MODEL slx_82d3541175fb
CONFIG AbsTol = auto
CONFIG EnableMultiTasking = off
CONFIG FixedStep = auto
CONFIG MaxStep = auto
CONFIG MinStep = auto
CONFIG RelTol = 1e-3
CONFIG SampleTimeConstraint = Unconstrained
CONFIG SolverName = VariableStepAuto
CONFIG StartTime = 0.0
CONFIG StopTime = 7
BLOCK [Reference] AC Voltage Source3  REF=spsACVoltageSourceLib/AC Voltage Source
  Commented = on
  LibrarySourceBlock = sps_lib/Sources/AC Voltage Source
  NameLocation = left
  SourceBlock = spsACVoltageSourceLib/AC Voltage Source
  SourceType = AC Voltage Source
BLOCK [BusSelector] Bus Selector1
  OutputSignals = Electrical torque Te (n m),Speed wm (rad/s)
BLOCK [Constant] CCW Direction
  Value = 0
BLOCK [Constant] CW Direction
BLOCK [Constant] Constant2
  Value = 0.6
BLOCK [Reference] Current Measurement  REF=spsCurrentMeasurementLib/Current Measurement
  LibrarySourceBlock = sps_lib/Sensors and Measurements/Current Measurement
  SourceBlock = spsCurrentMeasurementLib/Current Measurement
  SourceType = Current Measurement
  UserDataPersistent = on
BLOCK [Reference] Current Measurement1  REF=spsCurrentMeasurementLib/Current Measurement
  Commented = on
  LibrarySourceBlock = sps_lib/Sensors and Measurements/Current Measurement
  SourceBlock = spsCurrentMeasurementLib/Current Measurement
  SourceType = Current Measurement
  UserDataPersistent = on
BLOCK [Reference] Current Measurement2  REF=spsCurrentMeasurementLib/Current Measurement
  LibrarySourceBlock = sps_lib/Sensors and Measurements/Current Measurement
  SourceBlock = spsCurrentMeasurementLib/Current Measurement
  SourceType = Current Measurement
  UserDataPersistent = on
BLOCK [Reference] DC Machine1  REF=spsDCMachineLib/DC Machine
  LibrarySourceBlock = sps_lib/Electrical Machines/DC Machine
  SourceBlock = spsDCMachineLib/DC Machine
  SourceType = DC machine
BLOCK [Reference] DC Voltage Source  REF=spsDCVoltageSourceLib/DC Voltage Source
  LibrarySourceBlock = sps_lib/Sources/DC Voltage Source
  NameLocation = right
  SourceBlock = spsDCVoltageSourceLib/DC Voltage Source
  SourceType = DC Voltage Source
BLOCK [Reference] DC Voltage Source1  REF=spsDCVoltageSourceLib/DC Voltage Source
  LibrarySourceBlock = sps_lib/Sources/DC Voltage Source
  SourceBlock = spsDCVoltageSourceLib/DC Voltage Source
  SourceType = DC Voltage Source
BLOCK [Reference] Diode1  REF=spsDiodeLib/Diode
  LibrarySourceBlock = sps_lib/Power Electronics/Diode
  NameLocation = right
  SourceBlock = spsDiodeLib/Diode
  SourceType = Diode
BLOCK [Reference] Diode2  REF=spsDiodeLib/Diode
  LibrarySourceBlock = sps_lib/Power Electronics/Diode
  NameLocation = right
  SourceBlock = spsDiodeLib/Diode
  SourceType = Diode
BLOCK [Reference] Diode3  REF=spsDiodeLib/Diode
  LibrarySourceBlock = sps_lib/Power Electronics/Diode
  NameLocation = right
  SourceBlock = spsDiodeLib/Diode
  SourceType = Diode
BLOCK [Reference] Diode4  REF=spsDiodeLib/Diode
  LibrarySourceBlock = sps_lib/Power Electronics/Diode
  NameLocation = right
  SourceBlock = spsDiodeLib/Diode
  SourceType = Diode
BLOCK [Reference] Diode5  REF=spsDiodeLib/Diode
  Commented = on
  LibrarySourceBlock = sps_lib/Power Electronics/Diode
  NameLocation = right
  SourceBlock = spsDiodeLib/Diode
  SourceType = Diode
BLOCK [Reference] Diode6  REF=spsDiodeLib/Diode
  Commented = on
  LibrarySourceBlock = sps_lib/Power Electronics/Diode
  NameLocation = right
  SourceBlock = spsDiodeLib/Diode
  SourceType = Diode
BLOCK [Reference] Diode7  REF=spsDiodeLib/Diode
  Commented = on
  LibrarySourceBlock = sps_lib/Power Electronics/Diode
  NameLocation = right
  SourceBlock = spsDiodeLib/Diode
  SourceType = Diode
BLOCK [Reference] Diode8  REF=spsDiodeLib/Diode
  Commented = on
  LibrarySourceBlock = sps_lib/Power Electronics/Diode
  NameLocation = right
  SourceBlock = spsDiodeLib/Diode
  SourceType = Diode
BLOCK [Reference] Ground  REF=spsGroundLib/Ground
  LibrarySourceBlock = sps_lib/Utilities/Ground
  NameLocation = right
  SourceBlock = spsGroundLib/Ground
  SourceType = Ground
BLOCK [ManualSwitch] Manual Switch
BLOCK [ManualSwitch] Manual Switch1
  CurrentSetting = 0
BLOCK [Reference] Mosfet1  REF=spsMosfetLib/Mosfet
  LibrarySourceBlock = sps_lib/Power Electronics/Mosfet
  NameLocation = left
  SourceBlock = spsMosfetLib/Mosfet
  SourceType = Mosfet
BLOCK [Reference] Mosfet2  REF=spsMosfetLib/Mosfet
  LibrarySourceBlock = sps_lib/Power Electronics/Mosfet
  NameLocation = left
  SourceBlock = spsMosfetLib/Mosfet
  SourceType = Mosfet
BLOCK [Reference] Mosfet3  REF=spsMosfetLib/Mosfet
  LibrarySourceBlock = sps_lib/Power Electronics/Mosfet
  NameLocation = left
  SourceBlock = spsMosfetLib/Mosfet
  SourceType = Mosfet
BLOCK [Reference] Mosfet4  REF=spsMosfetLib/Mosfet
  LibrarySourceBlock = sps_lib/Power Electronics/Mosfet
  NameLocation = left
  SourceBlock = spsMosfetLib/Mosfet
  SourceType = Mosfet
BLOCK [Logic] NOT
  AllPortsSameDT = off
  IconShape = distinctive
  Operator = NOT
  OutDataTypeStr = boolean
BLOCK [Reference] PWM Generator  REF=eePwmGenerator/PWM Generator
  LibrarySourceBlock = ee_sl_lib/Pulse Width
Modulation/PWM Generator
  SourceBlock = eePwmGenerator/PWM Generator
  SourceType = PWM Generator
BLOCK [Product] Product
BLOCK [Product] Product1
BLOCK [Reference] Ramp  REF=simulink/Sources/Ramp
  NameLocation = left
  SourceBlock = simulink/Sources/Ramp
  SourceType = Ramp
BLOCK [Reference] Ramp1  REF=simulink/Sources/Ramp
  SourceBlock = simulink/Sources/Ramp
  SourceType = Ramp
BLOCK [Saturate] Saturation
  LowerLimit = 0
  NameLocation = left
  UpperLimit = 10
BLOCK [Saturate] Saturation1
  LowerLimit = 0
  UpperLimit = 0.8
BLOCK [Scope] Scope
  ActiveDisplayYMaximum = 127.17519359460283
  ActiveDisplayYMinimum = -14.130577066066978
  DataLoggingVariableName = ScopeData2
  Floating = off
  GraphicalSettings = {"AxesScalingProperties":{"AlignXAxis":"Center","AlignYAxis":"Center","AutoScaleXAxisLimits":false,"AxesScaling":"Manual","AxesScalingNumUpdates":10,"ExpandOnly":true,"ScaleAxesLimitsAtStop":false,"XAxisDataRange":100,"YAxisDataRange":80},"DisplayProperties":{"ColorOrder":["auto","auto","auto","auto","auto","auto","auto","auto","auto","auto","auto","auto","auto","auto","auto","auto","auto","auto",...<+2178ch>
  MultipleDisplayCache = [{"MaxYLimMag":127.17519359460283,"MaxYLimReal":127.17519359460283,"MinYLimMag":0,"MinYLimReal":-14.130577066066978,"PlotAsMagnitudePhase":false,"ShowGrid":true,"ShowLegend":true,"Title":"%<SignalLabel>","YLabel":""}]
  NameLocation = left
  NumInputPorts = 1
  ScopeFrameLocation = window
  ShowLegend = on
  WasSavedAsWebScope = on
  WindowPosition = [1.000000,41.000000,1920.000000,1017.000000,]
BLOCK [Scope] Scope1
  ActiveDisplayYMaximum = 205.7174886404658
  ActiveDisplayYMinimum = 197.20667546347846
  Floating = off
  GraphicalSettings = {"AxesScalingProperties":{"AlignXAxis":"Center","AlignYAxis":"Center","AutoScaleXAxisLimits":false,"AxesScaling":"Manual","AxesScalingNumUpdates":10,"ExpandOnly":true,"ScaleAxesLimitsAtStop":false,"XAxisDataRange":100,"YAxisDataRange":80},"DisplayProperties":{"ColorOrder":["auto","auto","auto","auto","auto","auto","auto","auto","auto","auto","auto","auto","auto","auto","auto","auto","auto","auto",...<+2026ch>
  MultipleDisplayCache = [{"MaxYLimMag":229.0419020090381,"MaxYLimReal":205.7174886404658,"MinYLimMag":0,"MinYLimReal":197.20667546347846,"PlotAsMagnitudePhase":false,"ShowGrid":true,"ShowLegend":false,"Title":"%<SignalLabel>","YLabel":""}]
  NumInputPorts = 1
  ScopeFrameLocation = window
  WasSavedAsWebScope = on
  WindowPosition = [0.000000,32.000000,1536.000000,801.000000,]
BLOCK [Scope] Scope12
  ActiveDisplayYMaximum = 9.5444979024542747
  ActiveDisplayYMinimum = -4.3267096598487811
  DataLoggingVariableName = ScopeData11
  Floating = off
  GraphicalSettings = {"Style":{"BackgroundColor":[0.12941176470588237,0.12941176470588237,0.12941176470588237],"AxesColor":[0.07058823529411765,0.07058823529411765,0.07058823529411765],"LabelsColor":[0.8509803921568627,0.8509803921568627,0.8509803921568627],"PreserveColors":false,"Visible":[true],"LineStyle":["-"],"LineWidth":[1.5],"BarWidth":[0.9],"LineColor":["auto"],"LineFaceAlpha":[1],"LineEdgeAlpha":[1],"Marker":...<+2017ch>
  MultipleDisplayCache = [{"MaxYLimMag":127.0240272759662,"MaxYLimReal":9.5444979024542747,"MinYLimMag":0,"MinYLimReal":-4.3267096598487811,"PlotAsMagnitudePhase":false,"ShowGrid":true,"ShowLegend":false,"Title":"%<SignalLabel>","YLabel":""}]
  NameLocation = right
  NumInputPorts = 1
  ScopeFrameLocation = window
  WasSavedAsWebScope = on
  WindowPosition = [0.000000,32.000000,1536.000000,801.000000,]
BLOCK [Scope] Scope2
  ActiveDisplayYMaximum = 25.20951403026401
  ActiveDisplayYMinimum = -226.88562627237616
  DataLoggingVariableName = ScopeData3
  Floating = off
  GraphicalSettings = {"Style":{"BackgroundColor":[0.12941176470588237,0.12941176470588237,0.12941176470588237],"AxesColor":[0.07058823529411765,0.07058823529411765,0.07058823529411765],"LabelsColor":[0.8509803921568627,0.8509803921568627,0.8509803921568627],"PreserveColors":false,"Visible":[true,true],"LineStyle":["-","-"],"LineWidth":[1.5,1.5],"BarWidth":[0.9,0.9],"LineColor":["auto","auto"],"LineFaceAlpha":[1,1],"Li...<+2069ch>
  MultipleDisplayCache = [{"MaxYLimMag":226.88562627237616,"MaxYLimReal":25.20951403026401,"MinYLimMag":0,"MinYLimReal":-226.88562627237616,"PlotAsMagnitudePhase":false,"ShowGrid":true,"ShowLegend":false,"Title":"%<SignalLabel>","YLabel":""}]
  NameLocation = right
  NumInputPorts = 1
  ScopeFrameLocation = window
  WasSavedAsWebScope = on
  WindowPosition = [488.000000,222.000000,560.000000,420.000000,]
BLOCK [Scope] Scope3
  ActiveDisplayYMaximum = 0.45210221887226021
  ActiveDisplayYMinimum = -4.2782265526615753
  DataLoggingVariableName = ScopeData4
  Floating = off
  GraphicalSettings = {"Style":{"BackgroundColor":[0.12941176470588237,0.12941176470588237,0.12941176470588237],"AxesColor":[0.07058823529411765,0.07058823529411765,0.07058823529411765],"LabelsColor":[0.8509803921568627,0.8509803921568627,0.8509803921568627],"PreserveColors":false,"Visible":[true,false,true,true,true,true,true],"LineStyle":["-","-","-","-","-","-","-"],"LineWidth":[1.5,1.5,1.5,1.5,1.5,1.5,1.5],"BarWidt...<+2576ch>
  MultipleDisplayCache = [{"MaxYLimMag":4.2572958943804515,"MaxYLimReal":0.45210221887226021,"MinYLimMag":0,"MinYLimReal":-4.2782265526615753,"PlotAsMagnitudePhase":false,"ShowGrid":true,"ShowLegend":true,"Title":"%<SignalLabel>","YLabel":""}]
  NameLocation = left
  NumInputPorts = 1
  ScopeFrameLocation = window
  ShowLegend = on
  WasSavedAsWebScope = on
  WindowPosition = [680.000000,330.000000,560.000000,420.000000,]
BLOCK [Scope] Scope4
  ActiveDisplayYMaximum = 190.37679133211168
  ActiveDisplayYMinimum = -17.897638486431848
  DataLoggingVariableName = ScopeData1
  Floating = off
  GraphicalSettings = {"AxesScalingProperties":{"AlignXAxis":"Center","AlignYAxis":"Center","AutoScaleXAxisLimits":false,"AxesScaling":"Manual","AxesScalingNumUpdates":10,"ExpandOnly":true,"ScaleAxesLimitsAtStop":false,"XAxisDataRange":100,"YAxisDataRange":80},"DisplayProperties":{"ColorOrder":["auto","auto","auto","auto","auto","auto","auto","auto","auto","auto","auto","auto","auto","auto","auto","auto","auto","auto",...<+2048ch>
  MultipleDisplayCache = [{"MaxYLimMag":239.23513324584667,"MaxYLimReal":190.37679133211168,"MinYLimMag":0,"MinYLimReal":-17.897638486431848,"PlotAsMagnitudePhase":false,"ShowGrid":true,"ShowLegend":false,"Title":"%<SignalLabel>","YLabel":""}]
  NumInputPorts = 1
  ScopeFrameLocation = window
  WasSavedAsWebScope = on
  WindowPosition = [1.000000,41.000000,1920.000000,1017.000000,]
BLOCK [Scope] Scope5
  ActiveDisplayYMaximum = 7.0075960496809362
  ActiveDisplayYMinimum = -1.20703950016334
  DataLoggingVariableName = ScopeData6
  Floating = off
  GraphicalSettings = {"Style":{"BackgroundColor":[0.12941176470588237,0.12941176470588237,0.12941176470588237],"AxesColor":[0.07058823529411765,0.07058823529411765,0.07058823529411765],"LabelsColor":[0.8509803921568627,0.8509803921568627,0.8509803921568627],"PreserveColors":false,"Visible":[true,true],"LineStyle":["-","-"],"LineWidth":[1.5,1.5],"BarWidth":[0.9,0.9],"LineColor":["auto","auto"],"LineFaceAlpha":[1,1],"Li...<+2168ch>
  MultipleDisplayCache = [{"MaxYLimMag":126.86904472662312,"MaxYLimReal":7.0075960496809362,"MinYLimMag":0,"MinYLimReal":-1.20703950016334,"PlotAsMagnitudePhase":false,"ShowGrid":true,"ShowLegend":false,"Title":"%<SignalLabel>","YLabel":""}]
  NameLocation = left
  NumInputPorts = 1
  ScopeFrameLocation = window
  WasSavedAsWebScope = on
  WindowPosition = [0.000000,32.000000,1536.000000,801.000000,]
BLOCK [Scope] Scope6
  ActiveDisplayYMaximum = 74.662265345837412
  ActiveDisplayYMinimum = -7.1846961495374888
  DataLoggingVariableName = ScopeData5
  Floating = off
  GraphicalSettings = {"Style":{"BackgroundColor":[0.12941176470588237,0.12941176470588237,0.12941176470588237],"AxesColor":[0.07058823529411765,0.07058823529411765,0.07058823529411765],"LabelsColor":[0.8509803921568627,0.8509803921568627,0.8509803921568627],"PreserveColors":false,"Visible":[true],"LineStyle":["-"],"LineWidth":[1.5],"BarWidth":[0.9],"LineColor":["auto"],"LineFaceAlpha":[1],"LineEdgeAlpha":[1],"Marker":...<+2015ch>
  MultipleDisplayCache = [{"MaxYLimMag":74.662265345837412,"MaxYLimReal":74.662265345837412,"MinYLimMag":0,"MinYLimReal":-7.1846961495374888,"PlotAsMagnitudePhase":false,"ShowGrid":true,"ShowLegend":false,"Title":"%<SignalLabel>","YLabel":""}]
  NumInputPorts = 1
  ScopeFrameLocation = window
  WasSavedAsWebScope = on
  WindowPosition = [1.000000,41.000000,1920.000000,1017.000000,]
BLOCK [Scope] Scope7
  ActiveDisplayYMaximum = 546.71556577016588
  ActiveDisplayYMinimum = -568.37134406736811
  Commented = on
  DataLoggingVariableName = ScopeData7
  Floating = off
  GraphicalSettings = {"AxesScalingProperties":{"AlignXAxis":"Center","AlignYAxis":"Center","AutoScaleXAxisLimits":false,"AxesScaling":"Manual","AxesScalingNumUpdates":10,"ExpandOnly":true,"ScaleAxesLimitsAtStop":false,"XAxisDataRange":100,"YAxisDataRange":80},"Cursors":{"CursorChannels":["auto","auto"],"Enabled":false,"Horizontal":true,"LinkToWaveform":true,"LockSpacing":false,"ShowMeasurement":true,"ShowPanel":false,...<+2357ch>
  MultipleDisplayCache = [{"MaxYLimMag":844.16576406883689,"MaxYLimReal":546.71556577016588,"MinYLimMag":0,"MinYLimReal":-568.37134406736811,"PlotAsMagnitudePhase":false,"ShowGrid":true,"ShowLegend":false,"Title":"%<SignalLabel>","YLabel":""}]
  NameLocation = right
  NumInputPorts = 1
  ScopeFrameLocation = window
  WasSavedAsWebScope = on
  WindowPosition = [0.000000,32.000000,1536.000000,801.000000,]
BLOCK [Scope] Scope8
  ActiveDisplayYMaximum = 14.547317732850114
  ActiveDisplayYMinimum = -130.92585959565105
  DataLoggingVariableName = ScopeData8
  Floating = off
  GraphicalSettings = {"Style":{"BackgroundColor":[0.12941176470588237,0.12941176470588237,0.12941176470588237],"AxesColor":[0.07058823529411765,0.07058823529411765,0.07058823529411765],"LabelsColor":[0.8509803921568627,0.8509803921568627,0.8509803921568627],"PreserveColors":false,"Visible":[true],"LineStyle":["-"],"LineWidth":[1.5],"BarWidth":[0.9],"LineColor":["auto"],"LineFaceAlpha":[1],"LineEdgeAlpha":[1],"Marker":...<+2025ch>
  MultipleDisplayCache = [{"MaxYLimMag":130.92585959565105,"MaxYLimReal":14.547317732850114,"MinYLimMag":0,"MinYLimReal":-130.92585959565105,"PlotAsMagnitudePhase":false,"ShowGrid":true,"ShowLegend":false,"Title":"%<SignalLabel>","YLabel":""}]
  NameLocation = right
  NumInputPorts = 1
  ScopeFrameLocation = window
  WasSavedAsWebScope = on
  WindowPosition = [1.000000,41.000000,1920.000000,1017.000000,]
BLOCK [Scope] Scope9
  ActiveDisplayYMaximum = 1.125
  ActiveDisplayYMinimum = -0.12499999999999997
  DataLoggingVariableName = ScopeData9
  Floating = off
  GraphicalSettings = {"Style":{"BackgroundColor":[0.12941176470588237,0.12941176470588237,0.12941176470588237],"AxesColor":[0.07058823529411765,0.07058823529411765,0.07058823529411765],"LabelsColor":[0.8509803921568627,0.8509803921568627,0.8509803921568627],"PreserveColors":false,"Visible":[true,false],"LineStyle":["-","-"],"LineWidth":[1.5,1.5],"BarWidth":[0.9,0.9],"LineColor":["auto","auto"],"LineFaceAlpha":[1,1],"L...<+2067ch>
  MultipleDisplayCache = [{"MaxYLimMag":1.125,"MaxYLimReal":1.125,"MinYLimMag":0,"MinYLimReal":-0.12499999999999997,"PlotAsMagnitudePhase":false,"ShowGrid":true,"ShowLegend":true,"Title":"%<SignalLabel>","YLabel":""}]
  NameLocation = left
  NumInputPorts = 2
  ScopeFrameLocation = window
  ShowLegend = on
  WasSavedAsWebScope = on
  WindowPosition = [1.000000,41.000000,1536.000000,801.000000,]
BLOCK [Reference] Series RLC Branch1  REF=spsSeriesRLCBranchLib/Series RLC Branch
  LibrarySourceBlock = sps_lib/Passives/Series RLC Branch
  SourceBlock = spsSeriesRLCBranchLib/Series RLC Branch
  SourceType = Series RLC Branch
BLOCK [Reference] Series RLC Branch3  REF=spsSeriesRLCBranchLib/Series RLC Branch
  LibrarySourceBlock = sps_lib/Passives/Series RLC Branch
  NameLocation = left
  SourceBlock = spsSeriesRLCBranchLib/Series RLC Branch
  SourceType = Series RLC Branch
BLOCK [Reference] Voltage Measurement2  REF=spsVoltageMeasurementLib/Voltage Measurement
  LibrarySourceBlock = sps_lib/Sensors and Measurements/Voltage Measurement
  SourceBlock = spsVoltageMeasurementLib/Voltage Measurement
  SourceType = Voltage Measurement
  UserDataPersistent = on
BLOCK [Reference] powergui2  REF=spspowerguiLib/powergui
  LibrarySourceBlock = sps_lib/powergui
  Priority = 1
  SourceBlock = spspowerguiLib/powergui
  SourceType = PSB option menu block
LINE AC Voltage Source3:rconn -> Current Measurement1:lconn
LINE Bus Selector1:1 -> Scope4:1
LINE Bus Selector1:2 -> Scope6:1
LINE CCW Direction:1 -> Manual Switch:2
LINE CW Direction:1 -> Manual Switch:1
LINE Constant2:1 -> Manual Switch1:2
LINE Current Measurement1:1 -> Scope7:1
LINE Current Measurement2:1 -> Scope8:1
LINE Current Measurement2:rconn -> DC Machine1:lconn
LINE Current Measurement:1 -> Scope12:1
LINE Current Measurement:lconn -> Series RLC Branch1:rconn
LINE Current Measurement:lconn -> Series RLC Branch3:lconn
LINE DC Machine1:1 -> Bus Selector1:1
LINE DC Voltage Source:lconn -> DC Machine1:rconn
LINE DC Voltage Source:rconn -> DC Machine1:lconn
LINE Diode1:1 -> Scope2:1
LINE Diode1:rconn -> Mosfet4:lconn
LINE Manual Switch1:1 -> PWM Generator:1
LINE Manual Switch:1 -> Mosfet3:1
LINE Manual Switch:1 -> NOT:1
LINE Manual Switch:1 -> Product:1
LINE Mosfet1:1 -> Scope3:1
LINE Mosfet3:1 -> Scope5:1
LINE Mosfet3:lconn -> Mosfet2:rconn
LINE Mosfet4:1 -> Scope:1
LINE Mosfet4:rconn -> Mosfet1:lconn
LINE NOT:1 -> Mosfet1:1
LINE NOT:1 -> Product1:2
LINE PWM Generator:1 -> Product1:1
LINE PWM Generator:1 -> Product:2
LINE Product1:1 -> Mosfet2:1
LINE Product1:1 -> Scope9:1
LINE Product:1 -> Mosfet4:1
LINE Product:1 -> Scope9:2
LINE Ramp1:1 -> Saturation1:1
LINE Ramp:1 -> Saturation:1
LINE Saturation1:1 -> Manual Switch1:1
LINE Saturation:1 -> DC Machine1:1
LINE Voltage Measurement2:1 -> Scope1:1
